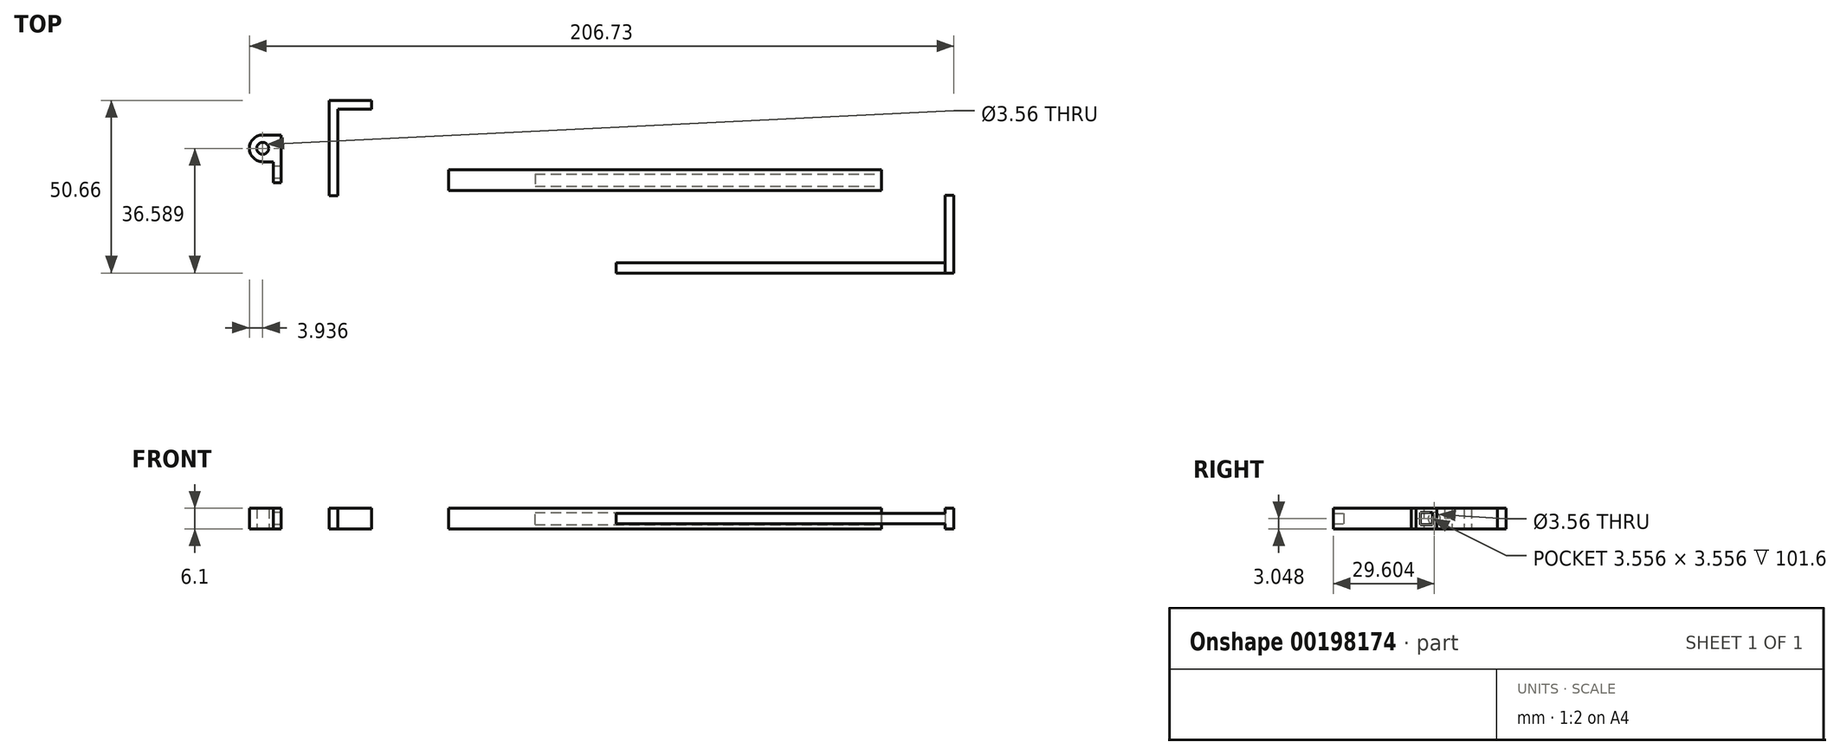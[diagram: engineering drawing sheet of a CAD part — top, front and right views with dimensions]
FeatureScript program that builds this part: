
annotation { "Feature Type Name" : "Feature", "Feature Type Description" : "" }
export const myFeature = defineFeature(function(context is Context, id is Id, definition is map)
    precondition{}
    {
        {
            var Q0;
            Q0=qCreatedBy(makeId("Top.planeOp"),FACE);
            var sketch = newSketch(context, id + "F0", { "sketchPlane" : qUnion([Q0])});
            skLineSegment(sketch, "E0", {"start": v(-26.88, 4.9) * mm, "end": v(-39.3, 4.9) * mm});
            skLineSegment(sketch, "E1", {"start": v(-39.3, 4.9) * mm, "end": v(-39.3, -23.03) * mm});
            skLineSegment(sketch, "E2", {"start": v(-39.3, -23.03) * mm, "end": v(-36.76, -23.03) * mm});
            skLineSegment(sketch, "E3", {"start": v(-36.76, -23.03) * mm, "end": v(-36.76, 2.37) * mm});
            skLineSegment(sketch, "E4", {"start": v(-36.76, 2.37) * mm, "end": v(-26.88, 2.37) * mm});
            skLineSegment(sketch, "E5", {"start": v(-26.88, 2.37) * mm, "end": v(-26.88, 4.9) * mm});
            skSolve(sketch);
        }
        {
            var Q0;
            Q0 = qSketchRegion(id + "F0", true);
            extrude(context, id + "F1", {"entities" : qUnion([Q0]), "depth" : 6.1 * mm});
        }
        {
            var Q0;
            Q0=qCreatedBy(makeId("Top.planeOp"),FACE);
            var sketch = newSketch(context, id + "F2", { "sketchPlane" : qUnion([Q0])});
            skLineSegment(sketch, "E6.bottom", {"start": v(-4.27, -21.48) * mm, "end": v(122.73, -21.48) * mm});
            skLineSegment(sketch, "E6.top", {"start": v(-4.27, -15.39) * mm, "end": v(122.73, -15.39) * mm});
            skLineSegment(sketch, "E6.left", {"start": v(-4.27, -21.48) * mm, "end": v(-4.27, -15.39) * mm});
            skLineSegment(sketch, "E6.right", {"start": v(122.73, -21.48) * mm, "end": v(122.73, -15.39) * mm});
            skSolve(sketch);
        }
        {
            var Q0;
            Q0 = qSketchRegion(id + "F2", true);
            extrude(context, id + "F3", {"entities" : qUnion([Q0]), "depth" : 6.1 * mm});
        }
        {
            var Q0;
            Q0=makeQuery(id+"F3.opExtrude","SWEPT_FACE",FACE,{"disambiguationData":[OSD([sQuery(id+"F2.wireOp",EDGE,"E6.right")])]});
            var sketch = newSketch(context, id + "F4", { "sketchPlane" : qUnion([Q0])});
            skLineSegment(sketch, "E7.bottom", {"start": v(-16.66, 1.27) * mm, "end": v(-20.21, 1.27) * mm});
            skLineSegment(sketch, "E7.top", {"start": v(-16.66, 4.83) * mm, "end": v(-20.21, 4.83) * mm});
            skLineSegment(sketch, "E7.left", {"start": v(-16.66, 1.27) * mm, "end": v(-16.66, 4.83) * mm});
            skLineSegment(sketch, "E7.right", {"start": v(-20.21, 1.27) * mm, "end": v(-20.21, 4.83) * mm});
            skPoint(sketch, "E7.middle", {"position": v(-18.44, 3.05) * mm});
            skPoint(sketch, "E7.middle.positionSnap0", {"position": v(-18.44, 6.1) * mm});
            skPoint(sketch, "E7.middle.positionSnap1", {"position": v(-15.39, 3.05) * mm});
            skPoint(sketch, "E7.centerSnap0", {"position": v(-18.44, 6.1) * mm});
            skPoint(sketch, "E7.centerSnap1", {"position": v(-15.39, 3.05) * mm});
            skSolve(sketch);
        }
        {
            var Q0;
            Q0 = qSketchRegion(id + "F4", true);
            extrude(context, id + "F5", {"entities" : qUnion([Q0]), "operationType" : NewBodyOperationType.REMOVE, "oppositeDirection" : true, "depth" : 101.6 * mm});
        }
        {
            var Q0;
            Q0=qCreatedBy(makeId("Top.planeOp"),FACE);
            var sketch = newSketch(context, id + "F6", { "sketchPlane" : qUnion([Q0])});
            skLineSegment(sketch, "E8", {"start": v(141.46, -45.75) * mm, "end": v(141.46, -25.43) * mm});
            skLineSegment(sketch, "E9", {"start": v(141.46, -25.43) * mm, "end": v(136.38, -25.43) * mm});
            skLineSegment(sketch, "E10", {"start": v(136.38, -25.43) * mm, "end": v(136.38, -22.89) * mm});
            skLineSegment(sketch, "E11", {"start": v(136.38, -22.89) * mm, "end": v(144, -22.89) * mm});
            skLineSegment(sketch, "E12", {"start": v(144, -22.89) * mm, "end": v(144, -45.75) * mm});
            skLineSegment(sketch, "E13", {"start": v(144, -45.75) * mm, "end": v(141.46, -45.75) * mm});
            skLineSegment(sketch, "E14", {"start": v(141.46, -25.43) * mm, "end": v(141.46, -22.89) * mm});
            skSolve(sketch);
        }
        {
            var Q0;
            Q0=makeQuery(id+"F6.imprint","IMPRINT",FACE,{"disambiguationData":[TD([[makeQuery(id+"F6.imprint","IMPRINT",EDGE,{"derivedFrom":sQuery(id+"F6.wireOp",EDGE,"E8")}),-1.0]])]});
            extrude(context, id + "F7", {"entities" : qUnion([Q0]), "depth" : 6.1 * mm});
        }
        {
            var Q0;
            Q0=makeQuery(id+"F7.opExtrude","SWEPT_FACE",FACE,{"disambiguationData":[OSD([sQuery(id+"F6.wireOp",EDGE,"E8")])]});
            var sketch = newSketch(context, id + "F8", { "sketchPlane" : qUnion([Q0])});
            skLineSegment(sketch, "E15.bottom", {"start": v(45.75, 4.57) * mm, "end": v(42.7, 4.57) * mm});
            skLineSegment(sketch, "E15.top", {"start": v(45.75, 1.52) * mm, "end": v(42.7, 1.52) * mm});
            skLineSegment(sketch, "E15.left", {"start": v(45.75, 4.57) * mm, "end": v(45.75, 1.52) * mm});
            skLineSegment(sketch, "E15.right", {"start": v(42.7, 4.57) * mm, "end": v(42.7, 1.52) * mm});
            skPoint(sketch, "E15.middle", {"position": v(44.22, 3.05) * mm});
            skPoint(sketch, "E15.middle.positionSnap0", {"position": v(45.75, 3.05) * mm});
            skPoint(sketch, "E15.centerSnap0", {"position": v(45.75, 3.05) * mm});
            skSolve(sketch);
        }
        {
            var Q0;
            Q0 = qSketchRegion(id + "F8", true);
            extrude(context, id + "F9", {"entities" : qUnion([Q0]), "operationType" : NewBodyOperationType.ADD, "depth" : 96.52 * mm});
        }
        {
            var Q0;
            Q0=qCreatedBy(makeId("Top.planeOp"),FACE);
            var sketch = newSketch(context, id + "F10", { "sketchPlane" : qUnion([Q0])});
            skLineSegment(sketch, "E16.bottom", {"start": v(-53.4, -19.2) * mm, "end": v(-55.75, -19.2) * mm});
            skLineSegment(sketch, "E16.top", {"start": v(-53.4, -5.22) * mm, "end": v(-55.75, -5.22) * mm});
            skLineSegment(sketch, "E16.left", {"start": v(-53.4, -19.2) * mm, "end": v(-53.4, -5.22) * mm});
            skLineSegment(sketch, "E16.right", {"start": v(-55.75, -19.2) * mm, "end": v(-55.75, -5.22) * mm});
            skCircle(sketch, "E17", {"center": v(-58.8, -9.16) * mm, "radius": 1.78 * mm});
            skArc(sketch, "E18", {"start": v(-58.8, -5.22) * mm, "mid": v(-62.73, -9.16) * mm, "end": v(-58.8, -13.1) * mm});
            skLineSegment(sketch, "E19", {"start": v(-58.8, -5.22) * mm, "end": v(-55.75, -5.22) * mm});
            skLineSegment(sketch, "E20", {"start": v(-55.75, -5.22) * mm, "end": v(-55.75, -13.1) * mm});
            skLineSegment(sketch, "E21", {"start": v(-55.75, -13.1) * mm, "end": v(-58.8, -13.1) * mm});
            skSolve(sketch);
        }
        {
            var Q0;
            Q0 = qSketchRegion(id + "F10", true);
            extrude(context, id + "F11", {"entities" : qUnion([Q0]), "depth" : 6.1 * mm});
        }
        {
            var Q0;
            Q0=makeQuery(id+"F11.opExtrude","SWEPT_FACE",FACE,{"disambiguationData":[OSD([sQuery(id+"F10.wireOp",EDGE,"E16.right")])]});
            var sketch = newSketch(context, id + "F12", { "sketchPlane" : qUnion([Q0])});
            skCircle(sketch, "E22", {"center": v(16.15, 3.05) * mm, "radius": 1.78 * mm});
            skPoint(sketch, "E22.centerSnap0", {"position": v(16.15, 0) * mm});
            skPoint(sketch, "E22.centerSnap1", {"position": v(19.2, 3.05) * mm});
            skSolve(sketch);
        }
        {
            var Q0;
            Q0 = qSketchRegion(id + "F12", true);
            var Q1;
            Q1=makeQuery(id+"F11.opExtrude","SWEPT_FACE",FACE,{"disambiguationData":[OSD([sQuery(id+"F10.wireOp",EDGE,"E16.left")])]});
            extrude(context, id + "F13", {"entities" : qUnion([Q0]), "operationType" : NewBodyOperationType.REMOVE, "endBound" : BoundingType.UP_TO_SURFACE, "oppositeDirection" : true, "endBoundEntityFace" : qUnion([Q1]), "depth" : 25.4 * mm});
        }
    });
